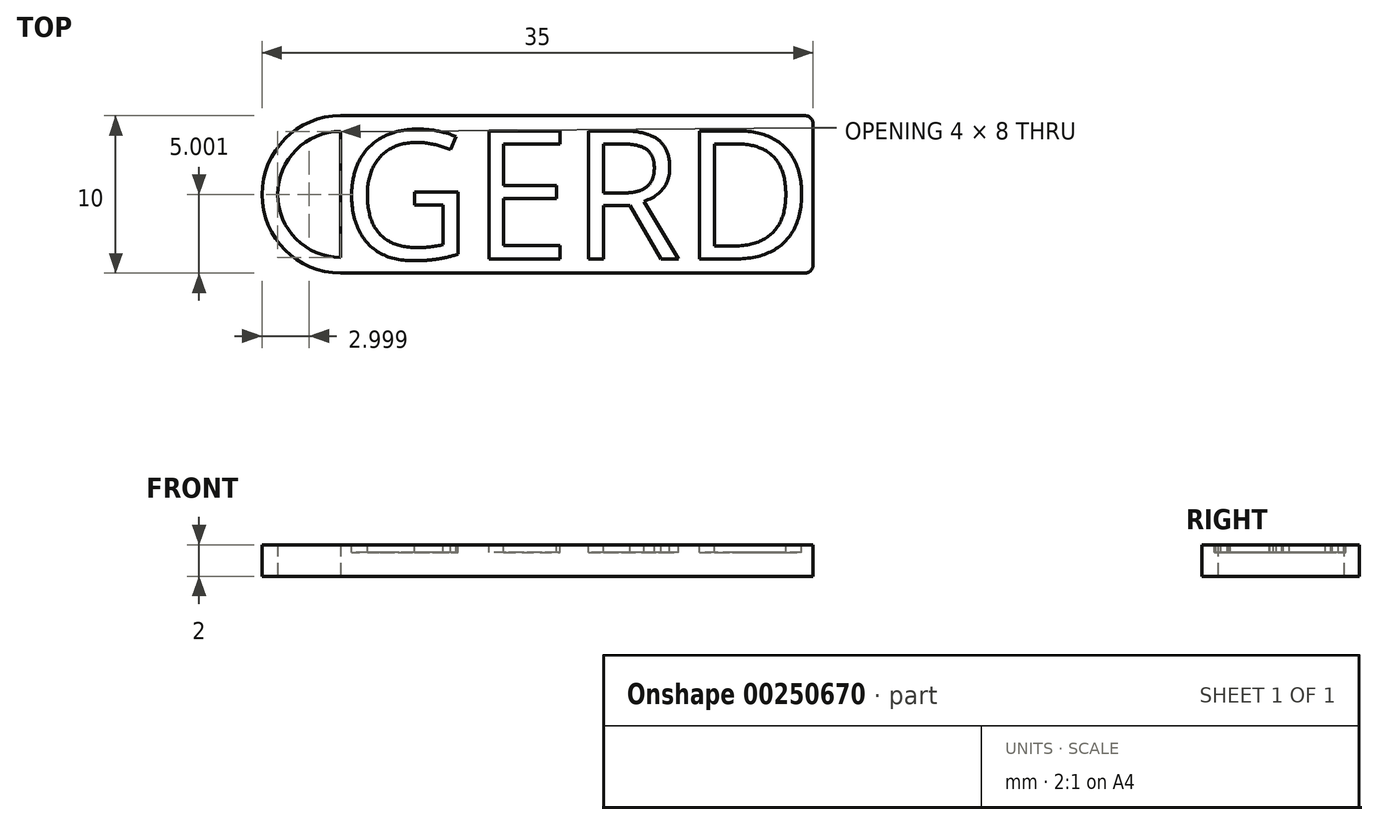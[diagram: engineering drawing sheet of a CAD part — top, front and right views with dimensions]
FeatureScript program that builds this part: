
annotation { "Feature Type Name" : "Feature", "Feature Type Description" : "" }
export const myFeature = defineFeature(function(context is Context, id is Id, definition is map)
    precondition{}
    {
        {
            var Q0;
            Q0=qCreatedBy(makeId("Top.planeOp"),FACE);
            var sketch = newSketch(context, id + "F0", { "sketchPlane" : qUnion([Q0])});
            skLineSegment(sketch, "E0.bottom", {"start": v(-5.27, 3.22) * mm, "end": v(24.73, 3.22) * mm});
            skLineSegment(sketch, "E0.top", {"start": v(-5.27, -6.78) * mm, "end": v(24.73, -6.78) * mm});
            skLineSegment(sketch, "E0.left", {"start": v(-5.27, 3.22) * mm, "end": v(-5.27, -6.78) * mm});
            skLineSegment(sketch, "E0.right", {"start": v(24.73, 3.22) * mm, "end": v(24.73, -6.78) * mm});
            skArc(sketch, "E1", {"start": v(-5.27, 3.22) * mm, "mid": v(-10.27, -1.78) * mm, "end": v(-5.27, -6.78) * mm});
            skArc(sketch, "E2", {"start": v(-5.27, 2.22) * mm, "mid": v(-9.27, -1.78) * mm, "end": v(-5.27, -5.78) * mm});
            skSolve(sketch);
        }
        {
            var Q0;
            Q0=qSketchRegion(id+"F0",true);
            extrude(context, id + "F4", {"entities" : qUnion([Q0]), "depth" : 2 * mm});
        }
        {
            var Q0;
            Q0=makeQuery(id+"F4.opExtrude","SWEPT_EDGE",EDGE,{"disambiguationData":[OSD([sQuery(id+"F0.wireOp",EDGE,"E0.top"),sQuery(id+"F0.wireOp",EDGE,"E0.right")])]});
            var Q1;
            Q1=makeQuery(id+"F4.opExtrude","SWEPT_EDGE",EDGE,{"disambiguationData":[OSD([sQuery(id+"F0.wireOp",EDGE,"E0.bottom"),sQuery(id+"F0.wireOp",EDGE,"E0.right")])]});
            fillet(context, id + "F1", {"entities" : qUnion([Q0, Q1]), "radius" : 0.5 * mm, "tangentPropagation" : true, "allowEdgeOverflow" : false});
        }
        {
            var Q0;
            Q0=makeQuery(id+"F4.opExtrude","CAP_FACE",FACE,{"disambiguationData":[OSD([sQuery(id+"F0.wireOp",EDGE,"E0.bottom"),sQuery(id+"F0.wireOp",EDGE,"E0.top"),sQuery(id+"F0.wireOp",EDGE,"E0.left"),sQuery(id+"F0.wireOp",EDGE,"E0.right"),sQuery(id+"F0.wireOp",EDGE,"E1"),sQuery(id+"F0.wireOp",EDGE,"E2")])],"isStart":false});
            var sketch = newSketch(context, id + "F2", { "sketchPlane" : qUnion([Q0])});
            skText(sketch, "E3", { "text": "GERD", "fontName": "OpenSans-Regular.ttf"});
            skPoint(sketch, "E4", {"position": v(-5.27, -1.78) * mm});
            skPoint(sketch, "E5", {"position": v(24.73, -1.78) * mm});
            const initialGuessF2  = {"E3": [-0.00527, -0.00588, 1, 0, 0.0082]};
            skSetInitialGuess(sketch, initialGuessF2);
            skSolve(sketch);
        }
        {
            var Q0;
            Q0 = qSketchRegion(id + "F2", true);
            extrude(context, id + "F3", {"entities" : qUnion([Q0]), "operationType" : NewBodyOperationType.REMOVE, "oppositeDirection" : true, "depth" : 0.5 * mm});
        }
    });
